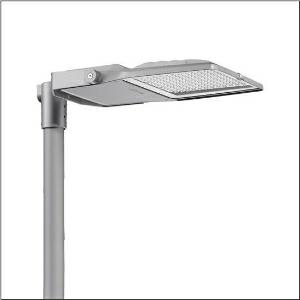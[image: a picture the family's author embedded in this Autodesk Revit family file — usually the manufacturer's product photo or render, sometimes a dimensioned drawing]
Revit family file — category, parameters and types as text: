
# Revit family: floodlight_fl_21_midi___pl61_5xa7781f4c3a_2346
name_source: partatom
category: Lighting Fixtures
units: mm (PartAtom-declared; Revit-internal decimal feet)

## family parameters
Cut with Voids When Loaded = No
Host = Face
Light Source = No
Part Type = Normal
Room Calculation Point = No
Round Connector Dimension = Use Diameter
Shared = No

## types (1)
- --- (1 x LED, 36650 lm, 270.2 W, 4000K)
    Apparent Load = 270 VA
    CIE Flux Codes = 33 65 98 100 100
    Color Rendering = 70
    Color Temperature = 4000K
    Default Elevation = 1800 mm
    Description = Floodlight FL 21 midi, floodlight, primary light control with lens, of PMMA, primary optical cover: protective disc, of toughened safety glass, transparent, light distribution: PL61, light emission: direct distribution, installation type: surface-mounted, LED, High Power LED, rated luminous flux: 36.650lm, luminous efficacy: 135lm/W, light colour: 740, colour temperature: 4000K, control gear: ECG iQ, control: optimised constant luminous flux control (CLO 2.0), Desk-Remote (wireless, voltage-free reading and setting of iQ features in the workshop via application-optimized NFC function/RFID function), Light-Fading, Smart-Wire, Night-Set, Lumen-Switch, Temp-Guard, Auto-Match, with terminal, 6-pole, mains connection: 220..240V, AC, 50/60Hz, start of lifetime: 270W, end of lifetime: 286W, reduction: 135W, luminaire housing, of diecast aluminium, powder-coated, Siteco® metallic grey (DB 702S), corrosivity category C5 according to DIN EN ISO 12944, mast bracket, of steel, galvanised, powder-coated, Siteco® metallic grey (DB 702S), protection rating (complete): IP66, insulation class (complete): insulation class I (protective earthing), certification: CE, protection symbol: D, impact resistance: IK08, permissible operating ambient temperature: -40..+40°C, permissible operating ambient temperature for outdoor applications: -40..+50°C, standard: DIN EN 12944, packaging unit: 1 piece

Light Distribution: PL61
    Height = 76 mm
    Lamp = 1 x LED
    Lamp Light Flux = 36650 lm
    Lamp Power = 270.2 W
    Lamp count = 1
    Length = 657 mm
    Luminous efficacy = 136 lm/W
    Manufacturer = Siteco
    ModVariant = No
    Model = 5XA7781F4C3A
    Number of Poles = 1
    OnlyDefault = Yes
    Power Factor = 1
    Product Name = Floodlight FL 21 midi | PL61
    Product group = floodlight | pylon top
    ProductGroupID = 6101
    Protection Class = Protection class I
    Protection Degree = IP 66
    RLX_Detail_Level = 1
    RlxData = <blob elided: 153333 chars, md5=3f627f5b>
    Socket = socket
    Standby Power = 0 W
    System Light Flux = 36650 lm
    System Power = 270 W
    Type Comments = factory setting: luminous flux: 100 % | dim-lin: 254 | 620 mA
    Type Image = l_1007123.jpg
    URL = http://relux.com
    VarID = @adj_016891
    Voltage = 0 V
    Weight = 0.00 kg
    Width = 442 mm

## geometry (parser evidence)
native form markers: Blend x4, Sweep x13
no freeform markers — native parametric forms only
